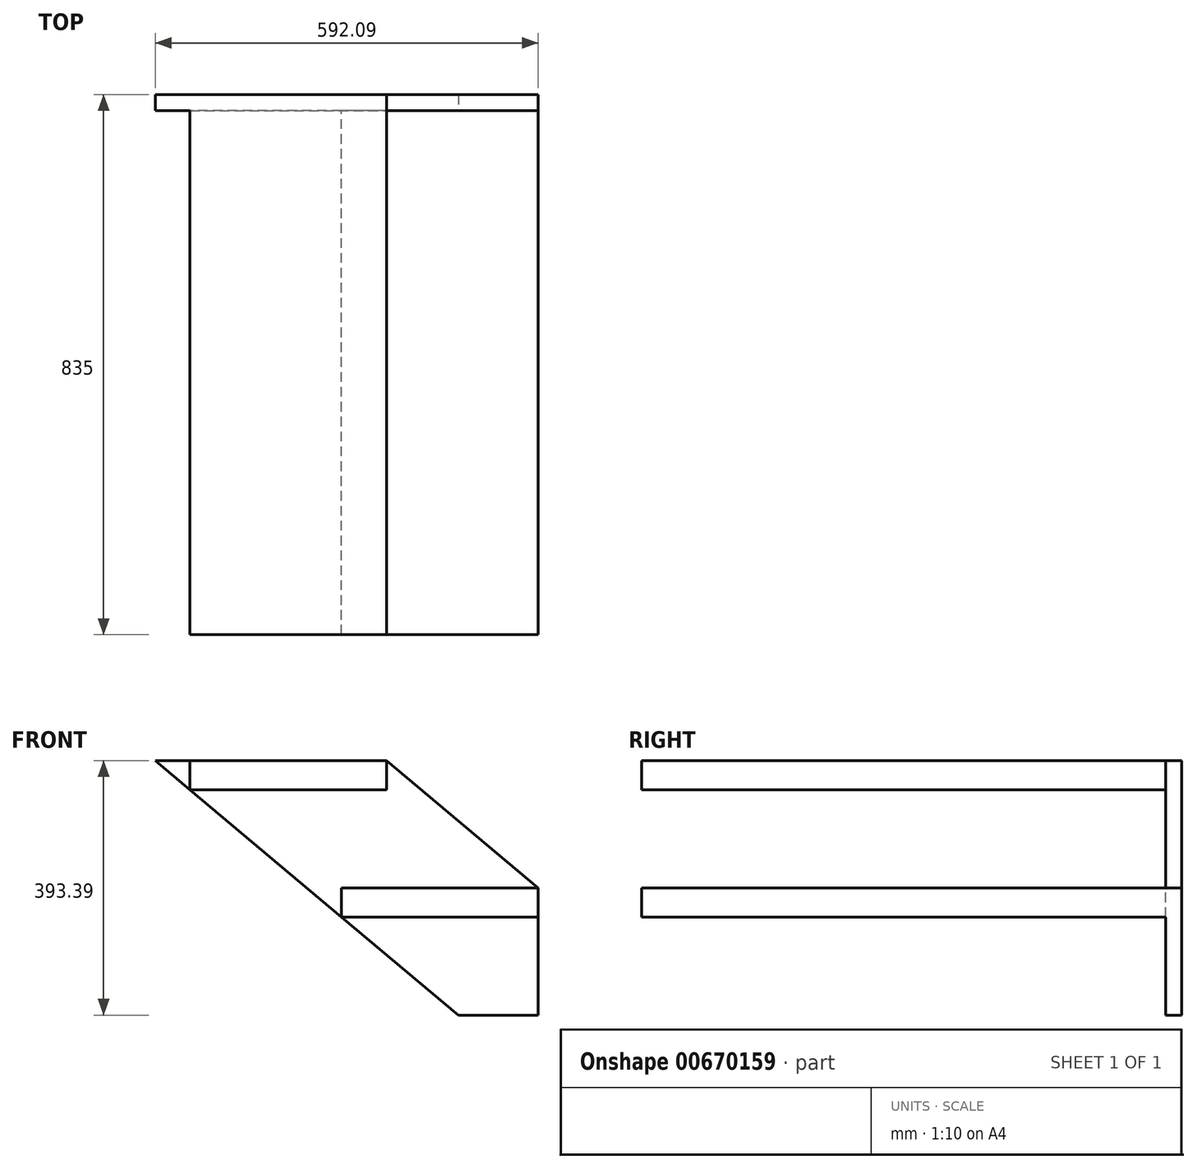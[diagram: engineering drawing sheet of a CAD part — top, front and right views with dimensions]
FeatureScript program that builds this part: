
annotation { "Feature Type Name" : "Feature", "Feature Type Description" : "" }
export const myFeature = defineFeature(function(context is Context, id is Id, definition is map)
    precondition{}
    {
        {
            var Q0;
            Q0=qCreatedBy(makeId("Front.planeOp"),FACE);
            var sketch = newSketch(context, id + "F0", { "sketchPlane" : qUnion([Q0])});
            skLineSegment(sketch, "E0", {"start": v(111.14, 0) * mm, "end": v(-357.68, 393.39) * mm});
            skLineSegment(sketch, "E1", {"start": v(-357.68, 393.39) * mm, "end": v(0, 393.39) * mm});
            skLineSegment(sketch, "E2", {"start": v(0, 393.39) * mm, "end": v(468.82, 0) * mm});
            skLineSegment(sketch, "E3", {"start": v(468.82, 0) * mm, "end": v(111.14, 0) * mm});
            skLineSegment(sketch, "E4", {"start": v(234.4, 196.7) * mm, "end": v(-123.27, 196.7) * mm});
            skLineSegment(sketch, "E5", {"start": v(234.4, 196.7) * mm, "end": v(234.4, 0) * mm});
            skLineSegment(sketch, "E6", {"start": v(-357.68, 393.39) * mm, "end": v(-140.82, 651.83) * mm, "construction": true});
            skLineSegment(sketch, "E7", {"start": v(-304.05, 348.39) * mm, "end": v(53.63, 348.39) * mm});
            skLineSegment(sketch, "E8", {"start": v(-69.64, 151.7) * mm, "end": v(234.4, 151.7) * mm});
            skLineSegment(sketch, "E9", {"start": v(-69.64, 151.7) * mm, "end": v(-69.64, 196.7) * mm});
            skLineSegment(sketch, "E10", {"start": v(-304.05, 348.39) * mm, "end": v(-304.05, 393.39) * mm});
            skLineSegment(sketch, "E11", {"start": v(0, 393.39) * mm, "end": v(0, 348.39) * mm});
            skLineSegment(sketch, "E12", {"start": v(200.4, 0) * mm, "end": v(200.4, 225.22) * mm});
            skSolve(sketch);
        }
        {
            var Q0;
            {var subQ6=sQuery(id+"F0.wireOp",EDGE,"E7");var subQ7=sQuery(id+"F0.wireOp",EDGE,"E2");var subQ8=makeQuery(id+"F0.imprint","INTERSECT",VERTEX,{"derivedFrom":[subQ7,subQ6]});Q0=makeQuery(id+"F0.imprint","IMPRINT",FACE,{"disambiguationData":[TD([[makeQuery(id+"F0.imprint","IMPRINT",EDGE,{"disambiguationData":[TD([[subQ8,-1.0]])],"derivedFrom":subQ7}),-1.0]])]});}
            var Q1;
            {var subQ3=sQuery(id+"F0.wireOp",EDGE,"E10");Q1=makeQuery(id+"F0.imprint","IMPRINT",FACE,{"disambiguationData":[TD([[makeQuery(id+"F0.imprint","IMPRINT",EDGE,{"derivedFrom":subQ3}),1.0]])]});}
            var Q2;
            {var subQ0=sQuery(id+"F0.wireOp",EDGE,"E11");Q2=makeQuery(id+"F0.imprint","IMPRINT",FACE,{"disambiguationData":[TD([[makeQuery(id+"F0.imprint","IMPRINT",EDGE,{"derivedFrom":subQ0}),1.0]])]});}
            var Q3;
            {var subQ0=sQuery(id+"F0.wireOp",EDGE,"E5");var subQ5=sQuery(id+"F0.wireOp",EDGE,"E8");var subQ6=makeQuery(id+"F0.imprint","INTERSECT",VERTEX,{"derivedFrom":[subQ0,subQ5]});Q3=makeQuery(id+"F0.imprint","IMPRINT",FACE,{"disambiguationData":[TD([[makeQuery(id+"F0.imprint","IMPRINT",EDGE,{"disambiguationData":[TD([[subQ6,1.0]])],"derivedFrom":subQ5}),1.0]])]});}
            var Q4;
            {var subQ0=sQuery(id+"F0.wireOp",EDGE,"E3");var subQ1=sQuery(id+"F0.wireOp",EDGE,"E0");var subQ2=makeQuery(id+"F0.imprint","INTERSECT",VERTEX,{"derivedFrom":[subQ1,subQ0]});Q4=makeQuery(id+"F0.imprint","IMPRINT",FACE,{"disambiguationData":[TD([[makeQuery(id+"F0.imprint","IMPRINT",EDGE,{"disambiguationData":[TD([[subQ2,1.0]])],"derivedFrom":subQ0}),-1.0]])]});}
            var Q5;
            {var subQ0=sQuery(id+"F0.wireOp",EDGE,"E9");Q5=makeQuery(id+"F0.imprint","IMPRINT",FACE,{"disambiguationData":[TD([[makeQuery(id+"F0.imprint","IMPRINT",EDGE,{"derivedFrom":subQ0}),-1.0]])]});}
            var Q6;
            {var subQ3=sQuery(id+"F0.wireOp",EDGE,"E9");Q6=makeQuery(id+"F0.imprint","IMPRINT",FACE,{"disambiguationData":[TD([[makeQuery(id+"F0.imprint","IMPRINT",EDGE,{"derivedFrom":subQ3}),1.0]])]});}
            var Q7;
            {var subQ2=sQuery(id+"F0.wireOp",EDGE,"E10");Q7=makeQuery(id+"F0.imprint","IMPRINT",FACE,{"disambiguationData":[TD([[makeQuery(id+"F0.imprint","IMPRINT",EDGE,{"derivedFrom":subQ2}),-1.0]])]});}
            var Q8;
            {var subQ0=sQuery(id+"F0.wireOp",EDGE,"E5");var subQ1=sQuery(id+"F0.wireOp",EDGE,"E3");var subQ2=makeQuery(id+"F0.imprint","INTERSECT",VERTEX,{"derivedFrom":[subQ1,subQ0]});Q8=makeQuery(id+"F0.imprint","IMPRINT",FACE,{"disambiguationData":[TD([[makeQuery(id+"F0.imprint","IMPRINT",EDGE,{"disambiguationData":[TD([[subQ2,-1.0]])],"derivedFrom":subQ1}),-1.0]])]});}
            var Q9;
            {var subQ1=sQuery(id+"F0.wireOp",EDGE,"E2");var subQ3=sQuery(id+"F0.wireOp",EDGE,"E12");var subQ4=makeQuery(id+"F0.imprint","INTERSECT",VERTEX,{"derivedFrom":[subQ1,subQ3]});Q9=makeQuery(id+"F0.imprint","IMPRINT",FACE,{"disambiguationData":[TD([[makeQuery(id+"F0.imprint","IMPRINT",EDGE,{"disambiguationData":[TD([[subQ4,1.0]])],"derivedFrom":subQ3}),-1.0]])]});}
            extrude(context, id + "F1", {"entities" : qUnion([Q0, Q1, Q2, Q3, Q4, Q5, Q6, Q7, Q8, Q9]), "oppositeDirection" : true, "depth" : 25 * mm, "offsetDistance" : 25 * mm});
        }
        {
            var Q0;
            {var subQ2=sQuery(id+"F0.wireOp",EDGE,"E10");Q0=makeQuery(id+"F0.imprint","IMPRINT",FACE,{"disambiguationData":[TD([[makeQuery(id+"F0.imprint","IMPRINT",EDGE,{"derivedFrom":subQ2}),-1.0]])]});}
            var Q1;
            {var subQ0=sQuery(id+"F0.wireOp",EDGE,"E9");Q1=makeQuery(id+"F0.imprint","IMPRINT",FACE,{"disambiguationData":[TD([[makeQuery(id+"F0.imprint","IMPRINT",EDGE,{"derivedFrom":subQ0}),-1.0]])]});}
            var Q2;
            {var subQ0=sQuery(id+"F0.wireOp",EDGE,"E5");var subQ5=sQuery(id+"F0.wireOp",EDGE,"E8");var subQ6=makeQuery(id+"F0.imprint","INTERSECT",VERTEX,{"derivedFrom":[subQ0,subQ5]});Q2=makeQuery(id+"F0.imprint","IMPRINT",FACE,{"disambiguationData":[TD([[makeQuery(id+"F0.imprint","IMPRINT",EDGE,{"disambiguationData":[TD([[subQ6,1.0]])],"derivedFrom":subQ5}),1.0]])]});}
            extrude(context, id + "F2", {"entities" : qUnion([Q0, Q1, Q2]), "operationType" : NewBodyOperationType.ADD, "depth" : 810 * mm, "offsetDistance" : 25 * mm});
        }
    });
